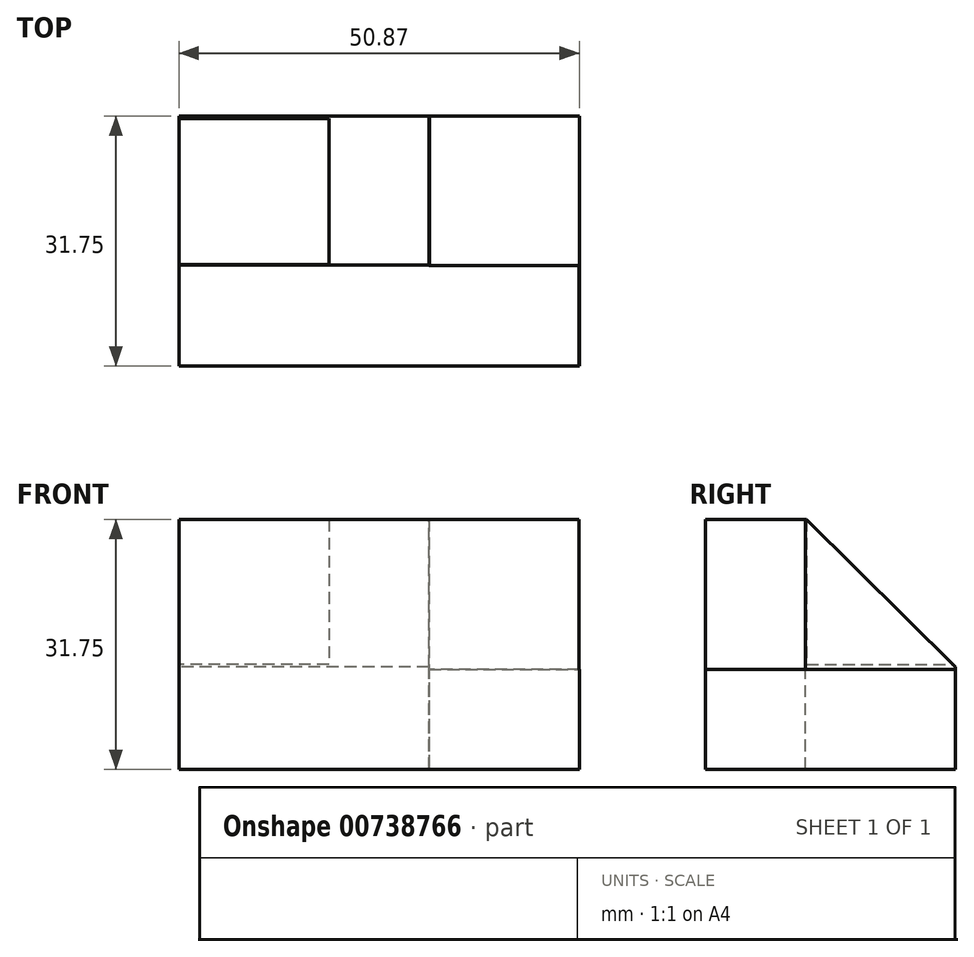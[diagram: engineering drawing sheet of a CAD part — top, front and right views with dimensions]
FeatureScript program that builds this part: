
annotation { "Feature Type Name" : "Feature", "Feature Type Description" : "" }
export const myFeature = defineFeature(function(context is Context, id is Id, definition is map)
    precondition{}
    {
        {
            var Q0;
            Q0=qCreatedBy(makeId("Front.planeOp"),FACE);
            var sketch = newSketch(context, id + "F0", { "sketchPlane" : qUnion([Q0])});
            skLineSegment(sketch, "E0", {"start": v(0, 0) * mm, "end": v(0, 31.75) * mm});
            skLineSegment(sketch, "E1", {"start": v(0, 31.75) * mm, "end": v(50.8, 31.75) * mm});
            skLineSegment(sketch, "E2", {"start": v(50.8, 31.75) * mm, "end": v(50.8, 0) * mm});
            skLineSegment(sketch, "E3", {"start": v(50.8, 0) * mm, "end": v(0, 0) * mm});
            skSolve(sketch);
        }
        {
            var Q0;
            Q0 = qSketchRegion(id + "F0", true);
            extrude(context, id + "F1", {"entities" : qUnion([Q0]), "oppositeDirection" : true, "depth" : 31.75 * mm, "offsetDistance" : 25.4 * mm});
        }
        {
            var Q0;
            Q0=qCreatedBy(makeId("Right.planeOp"),FACE);
            var sketch = newSketch(context, id + "F2", { "sketchPlane" : qUnion([Q0])});
            skLineSegment(sketch, "E4", {"start": v(12.87, 32.4) * mm, "end": v(12.87, 13.36) * mm});
            skLineSegment(sketch, "E5", {"start": v(12.87, 13.36) * mm, "end": v(31.92, 13.36) * mm});
            skLineSegment(sketch, "E6", {"start": v(31.92, 13.36) * mm, "end": v(31.92, 32.4) * mm});
            skLineSegment(sketch, "E7", {"start": v(31.92, 32.4) * mm, "end": v(12.87, 32.4) * mm});
            skSolve(sketch);
        }
        {
            var Q0;
            Q0 = qSketchRegion(id + "F2", true);
            extrude(context, id + "F3", {"entities" : qUnion([Q0]), "operationType" : NewBodyOperationType.REMOVE, "depth" : 19.05 * mm, "offsetDistance" : 25.4 * mm});
        }
        {
            var Q0;
            Q0=qCreatedBy(makeId("Top.planeOp"),FACE);
            var sketch = newSketch(context, id + "F4", { "sketchPlane" : qUnion([Q0])});
            skLineSegment(sketch, "E8", {"start": v(31.75, 31.79) * mm, "end": v(31.75, 12.74) * mm});
            skLineSegment(sketch, "E9", {"start": v(31.75, 12.74) * mm, "end": v(50.8, 12.74) * mm});
            skLineSegment(sketch, "E10", {"start": v(50.8, 12.74) * mm, "end": v(50.8, 31.79) * mm});
            skLineSegment(sketch, "E11", {"start": v(50.8, 31.79) * mm, "end": v(31.75, 31.79) * mm});
            skSolve(sketch);
        }
        {
            var Q0;
            Q0 = qSketchRegion(id + "F4", true);
            extrude(context, id + "F5", {"entities" : qUnion([Q0]), "operationType" : NewBodyOperationType.REMOVE, "endBound" : BoundingType.THROUGH_ALL, "depth" : 25.4 * mm, "offsetDistance" : 25.4 * mm});
        }
        {
            var Q0;
            Q0=qCreatedBy(makeId("Front.planeOp"),FACE);
            var sketch = newSketch(context, id + "F6", { "sketchPlane" : qUnion([Q0])});
            skLineSegment(sketch, "E12", {"start": v(50.87, 0) * mm, "end": v(50.87, 12.7) * mm});
            skLineSegment(sketch, "E13", {"start": v(50.87, 12.7) * mm, "end": v(31.82, 12.7) * mm});
            skLineSegment(sketch, "E14", {"start": v(31.82, 12.7) * mm, "end": v(31.82, 0) * mm});
            skLineSegment(sketch, "E15", {"start": v(31.82, 0) * mm, "end": v(50.87, 0) * mm});
            skSolve(sketch);
        }
        {
            var Q0;
            Q0 = qSketchRegion(id + "F6", true);
            extrude(context, id + "F7", {"entities" : qUnion([Q0]), "operationType" : NewBodyOperationType.ADD, "oppositeDirection" : true, "depth" : 31.75 * mm, "offsetDistance" : 25.4 * mm});
        }
        {
            var Q0;
            Q0=qCreatedBy(makeId("Right.planeOp"),FACE);
            var sketch = newSketch(context, id + "F8", { "sketchPlane" : qUnion([Q0])});
            skLineSegment(sketch, "E16", {"start": v(12.78, 31.82) * mm, "end": v(31.83, 12.97) * mm});
            skLineSegment(sketch, "E17", {"start": v(31.83, 12.97) * mm, "end": v(31.83, 32.02) * mm});
            skLineSegment(sketch, "E18", {"start": v(31.83, 32.02) * mm, "end": v(12.78, 31.82) * mm});
            skSolve(sketch);
        }
        {
            var Q0;
            Q0 = qSketchRegion(id + "F8", true);
            extrude(context, id + "F9", {"entities" : qUnion([Q0]), "operationType" : NewBodyOperationType.REMOVE, "endBound" : BoundingType.THROUGH_ALL, "depth" : 25.4 * mm, "offsetDistance" : 25.4 * mm});
        }
    });
